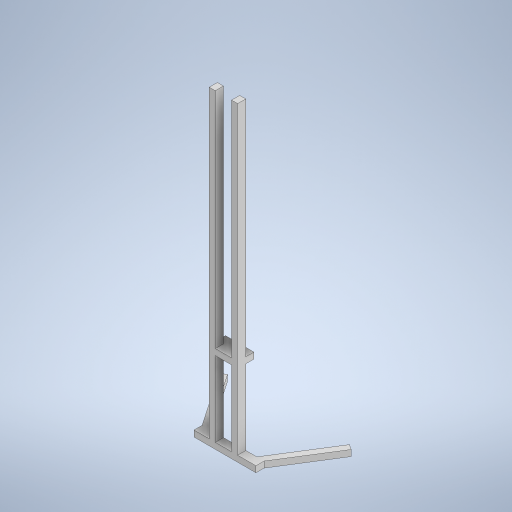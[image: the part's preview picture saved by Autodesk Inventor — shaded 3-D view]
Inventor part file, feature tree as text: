
AUTODESK INVENTOR PART (.ipt)
format: ipt  version: 2023 (Build 270158000, 158)  size: 299,008 bytes
history: native  units: mm
features: extrude x3, sketch x3, other x1
ambient origin geometry x8: Origin, YZ Plane, XZ Plane, XY Plane, X Axis, Y Axis, Z Axis, Center Point
bodies: Body1 (feature_tree)
feature tree (7):
  other  "Твердое тело1"
  extrude  "Выдавливание1"  Depth=110.0mm
  extrude  "Выдавливание2"  Depth=15.0mm
  extrude  "Выдавливание3"  Depth=30.0mm
  sketch  "Эскиз1"
  sketch  "Эскиз2"
  sketch  "Эскиз3"
